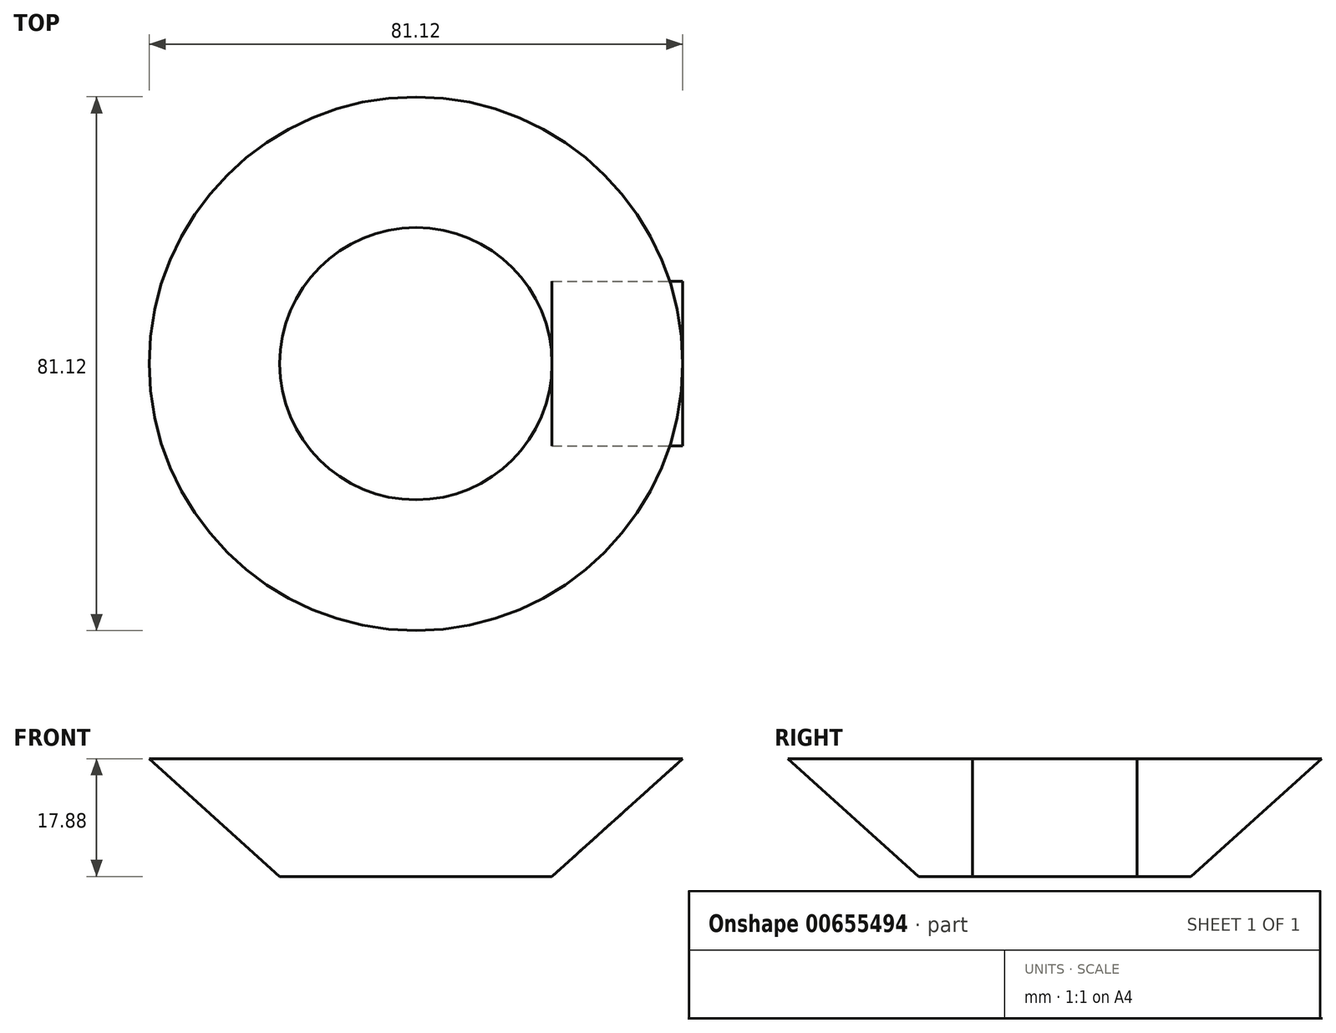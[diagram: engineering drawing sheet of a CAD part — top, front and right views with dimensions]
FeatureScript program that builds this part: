
annotation { "Feature Type Name" : "Feature", "Feature Type Description" : "" }
export const myFeature = defineFeature(function(context is Context, id is Id, definition is map)
    precondition{}
    {
        {
            var Q0;
            Q0=qCreatedBy(makeId("Top.planeOp"),FACE);
            var sketch = newSketch(context, id + "F0", { "sketchPlane" : qUnion([Q0])});
            skCircle(sketch, "E0", {"center": v(0, 0) * mm, "radius": 20.7 * mm});
            skSolve(sketch);
        }
        {
            var Q0;
            Q0=qCreatedBy(makeId("Front.planeOp"),FACE);
            var sketch = newSketch(context, id + "F1", { "sketchPlane" : qUnion([Q0])});
            skLineSegment(sketch, "E1", {"start": v(20.7, 0) * mm, "end": v(40.56, 17.88) * mm});
            skLineSegment(sketch, "E2.0", {"start": v(-20.7, 0) * mm, "end": v(20.7, 0) * mm});
            skSolve(sketch);
        }
        {
            var Q0;
            Q0=qCreatedBy(makeId("Front.planeOp"),FACE);
            var sketch = newSketch(context, id + "F2", { "sketchPlane" : qUnion([Q0])});
            skLineSegment(sketch, "E3", {"start": v(0, 0) * mm, "end": v(0, 36.86) * mm});
            skSolve(sketch);
        }
        {
            var Q0;
            Q0=sQuery(id+"F1.wireOp",EDGE,"E1");
            extrude(context, id + "F3", {"bodyType" : ToolBodyType.SURFACE, "surfaceEntities" : qUnion([Q0]), "endBound" : BoundingType.SYMMETRIC, "depth" : 25 * mm, "offsetDistance" : 25 * mm});
        }
        {
            var Q0;
            Q0 = qSketchRegion(id + "F1", true);
            var Q1;
            Q1=sQuery(id+"F1.wireOp",EDGE,"E1");
            var Q2;
            Q2=sQuery(id+"F2.wireOp",EDGE,"E3");
            revolve(context, id + "F4", {"bodyType" : ToolBodyType.SURFACE, "entities" : qUnion([Q0]), "surfaceEntities" : qUnion([Q1]), "axis" : qUnion([Q2]), "revolveType" : RevolveType.FULL});
        }
    });
